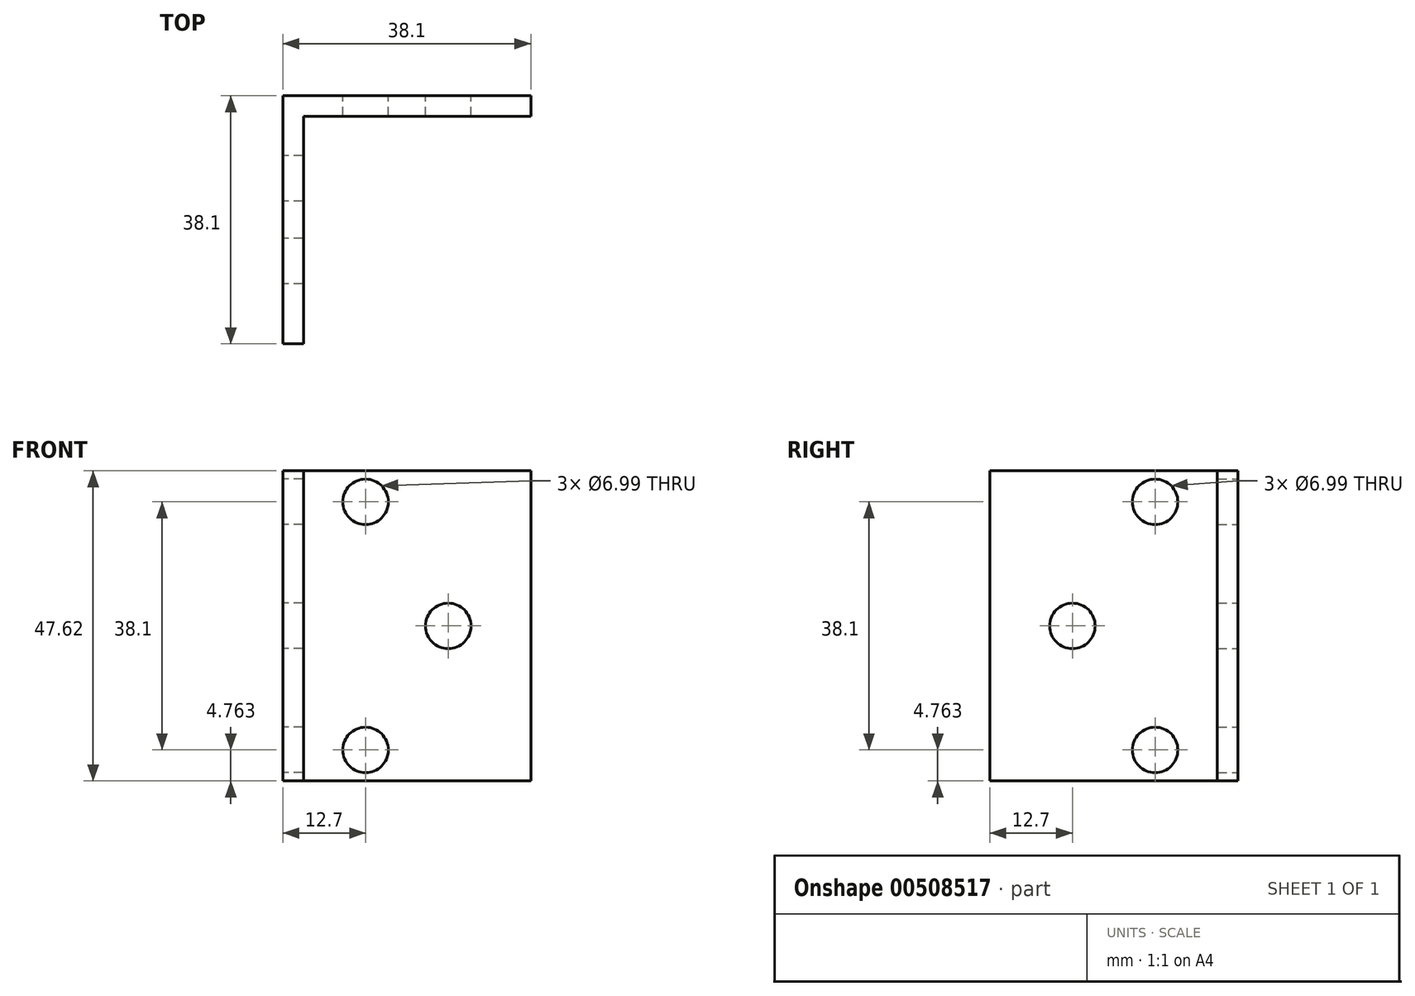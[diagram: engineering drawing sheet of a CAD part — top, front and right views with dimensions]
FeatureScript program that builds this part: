
annotation { "Feature Type Name" : "Feature", "Feature Type Description" : "" }
export const myFeature = defineFeature(function(context is Context, id is Id, definition is map)
    precondition{}
    {
        {
            var Q0;
            Q0=qCreatedBy(makeId("Top.planeOp"),FACE);
            var sketch = newSketch(context, id + "F0", { "sketchPlane" : qUnion([Q0])});
            skLineSegment(sketch, "E0.bottom", {"start": v(0, 0) * mm, "end": v(38.1, 0) * mm});
            skLineSegment(sketch, "E0.top", {"start": v(3.18, -3.18) * mm, "end": v(38.1, -3.18) * mm});
            skLineSegment(sketch, "E0.left", {"start": v(0, 0) * mm, "end": v(0, -3.18) * mm});
            skLineSegment(sketch, "E0.right", {"start": v(38.1, 0) * mm, "end": v(38.1, -3.18) * mm});
            skLineSegment(sketch, "E1.top", {"start": v(0, -38.1) * mm, "end": v(3.18, -38.1) * mm});
            skLineSegment(sketch, "E1.left", {"start": v(0, -3.18) * mm, "end": v(0, -38.1) * mm});
            skLineSegment(sketch, "E1.right", {"start": v(3.18, -3.18) * mm, "end": v(3.18, -38.1) * mm});
            skSolve(sketch);
        }
        {
            var Q0;
            Q0 = qSketchRegion(id + "F0", true);
            extrude(context, id + "F1", {"entities" : qUnion([Q0]), "depth" : 47.62 * mm, "offsetDistance" : 25.4 * mm});
        }
        {
            var Q0;
            Q0=makeQuery(id+"F1.opExtrude","SWEPT_FACE",FACE,{"disambiguationData":[OSD([sQuery(id+"F0.wireOp",EDGE,"E0.bottom")])]});
            var sketch = newSketch(context, id + "F2", { "sketchPlane" : qUnion([Q0])});
            skCircle(sketch, "E2", {"center": v(-12.7, 42.86) * mm, "radius": 3.5 * mm});
            skCircle(sketch, "E3", {"center": v(-12.7, 4.76) * mm, "radius": 3.5 * mm});
            skCircle(sketch, "E4", {"center": v(-25.4, 23.81) * mm, "radius": 3.5 * mm});
            skLineSegment(sketch, "E5", {"start": v(-12.7, 47.63) * mm, "end": v(-12.7, 0) * mm, "construction": true});
            skLineSegment(sketch, "E6", {"start": v(-25.4, 47.63) * mm, "end": v(-25.4, 0) * mm, "construction": true});
            skSolve(sketch);
        }
        {
            var Q0;
            Q0=makeQuery(id+"F2.imprint","IMPRINT",FACE,{"disambiguationData":[TD([[makeQuery(id+"F2.imprint","IMPRINT",EDGE,{"derivedFrom":sQuery(id+"F2.wireOp",EDGE,"E2")}),1.0]])]});
            var Q1;
            Q1=makeQuery(id+"F2.imprint","IMPRINT",FACE,{"disambiguationData":[TD([[makeQuery(id+"F2.imprint","IMPRINT",EDGE,{"derivedFrom":sQuery(id+"F2.wireOp",EDGE,"E4")}),1.0]])]});
            var Q2;
            Q2=makeQuery(id+"F2.imprint","IMPRINT",FACE,{"disambiguationData":[TD([[makeQuery(id+"F2.imprint","IMPRINT",EDGE,{"derivedFrom":sQuery(id+"F2.wireOp",EDGE,"E3")}),1.0]])]});
            extrude(context, id + "F3", {"entities" : qUnion([Q0, Q1, Q2]), "operationType" : NewBodyOperationType.REMOVE, "oppositeDirection" : true, "depth" : 25.4 * mm, "offsetDistance" : 25.4 * mm});
        }
        {
            var Q0;
            Q0=makeQuery(id+"F1.opExtrude","SWEPT_FACE",FACE,{"disambiguationData":[OSD([sQuery(id+"F0.wireOp",EDGE,"E0.left"),sQuery(id+"F0.wireOp",EDGE,"E1.left")])]});
            var sketch = newSketch(context, id + "F4", { "sketchPlane" : qUnion([Q0])});
            skCircle(sketch, "E7", {"center": v(12.7, 4.76) * mm, "radius": 3.5 * mm});
            skCircle(sketch, "E8", {"center": v(12.7, 42.86) * mm, "radius": 3.5 * mm});
            skCircle(sketch, "E9", {"center": v(25.4, 23.81) * mm, "radius": 3.5 * mm});
            skLineSegment(sketch, "E10", {"start": v(12.7, 0) * mm, "end": v(12.7, 47.63) * mm, "construction": true});
            skLineSegment(sketch, "E11", {"start": v(25.4, 0) * mm, "end": v(25.4, 47.63) * mm, "construction": true});
            skSolve(sketch);
        }
        {
            var Q0;
            Q0=makeQuery(id+"F4.imprint","IMPRINT",FACE,{"disambiguationData":[TD([[makeQuery(id+"F4.imprint","IMPRINT",EDGE,{"derivedFrom":sQuery(id+"F4.wireOp",EDGE,"E8")}),1.0]])]});
            var Q1;
            Q1=makeQuery(id+"F4.imprint","IMPRINT",FACE,{"disambiguationData":[TD([[makeQuery(id+"F4.imprint","IMPRINT",EDGE,{"derivedFrom":sQuery(id+"F4.wireOp",EDGE,"E9")}),1.0]])]});
            var Q2;
            Q2=makeQuery(id+"F4.imprint","IMPRINT",FACE,{"disambiguationData":[TD([[makeQuery(id+"F4.imprint","IMPRINT",EDGE,{"derivedFrom":sQuery(id+"F4.wireOp",EDGE,"E7")}),1.0]])]});
            extrude(context, id + "F5", {"entities" : qUnion([Q0, Q1, Q2]), "operationType" : NewBodyOperationType.REMOVE, "oppositeDirection" : true, "depth" : 25.4 * mm, "offsetDistance" : 25.4 * mm});
        }
    });
